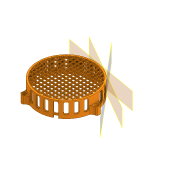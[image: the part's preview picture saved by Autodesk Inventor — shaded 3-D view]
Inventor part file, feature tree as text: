
AUTODESK INVENTOR PART (.ipt)
format: ipt  version: 2020.3 (Build 243373000, 373)  size: 1,350,656 bytes
history: native  units: mm
features: other x23, extrude x10, sketch x7, plane x3, pattern_circular x3
ambient origin geometry x8: Origin, YZ Plane, XZ Plane, XY Plane, X Axis, Y Axis, Z Axis, Center Point
bodies: Body1 (feature_tree)
feature tree (46):
  sketch  "Sketch1"  dims[d0=95.0mm d1=120.0deg]
  extrude  "Extrusion9"  TaperAngle=120.0deg  [1 undecoded]
  extrude  "Extrusion13"  Depth=16.0mm
  extrude  "Extrusion14"  Depth=6.5mm
  extrude  "Extrusion16"  Depth=10.0mm
  extrude  "Extrusion17"  Depth=1.2mm
  plane  "Work Plane5"
  plane  "Work Plane6"
  plane  "Work Plane7"
  sketch  "Sketch12"  dims[d4=3.4mm d5=6.5mm]
  sketch  "Sketch13"  dims[d7=10.0mm d8=3.6mm]
  sketch  "Sketch14"  dims[d9=2.4mm d10=1.2mm]
  extrude  "Extrusion21"  Depth=9.8mm
  extrude  "Extrusion22"  Depth=2.0mm
  extrude  "Extrusion23"  Depth=2.0mm
  sketch  "Sketch15"  dims[d13=30.0mm d15=360.0deg d17=9.8mm]
  sketch  "Sketch16"  dims[d18=12.0mm d19=2.0mm d20=6.0mm d21=2.0mm d23=60.0deg d24=6.1mm d25=8.0mm d26=6.1mm d27=60.0deg d28=3.490659mm d29=3.490659mm d56=40.0mm d57=60.0mm d58=3.2mm d59=1.3mm d60=1.0mm d61=1.0mm d62=1.3mm d64=3.0mm d65=8.0mm d66=6.0mm d74=90.0mm d75=26.0mm d76=0.0mm d83=4.2mm d84=0.0mm d85=8.4mm d86=0.0mm d99=12.5mm d100=0.0mm d101=6.5mm d102=6.0mm d103=6.0mm d104=3.0mm d105=0.0mm d115=4.0mm d116=4.0mm d122=90.0deg d123=90.0deg d124=90.0deg d126=5.5mm d127=5.5mm d128=5.5mm d129=10.0mm d130=0.0mm d131=10.0mm d132=0.0mm d133=10.0mm d134=0.0mm d137=18.0mm d138=2.0mm d141=240.0mm d142=360.0deg d191=2.0mm d192=0.0mm d194=95.0mm d195=90.0mm d198=1.0mm d199=5.0mm d200=1.0mm d201=5.0mm d202=1.0mm d203=5.0mm d204=1.0mm d205=5.0mm d206=1.0mm d207=5.0mm d208=1.0mm d209=5.0mm d210=1.0mm d211=1.0mm d212=5.0mm d213=1.0mm d214=5.0mm d215=1.0mm d216=5.0mm d217=1.0mm d218=5.0mm d219=1.0mm d220=5.0mm d221=1.0mm d222=5.0mm d223=1.0mm d224=5.0mm d225=1.0mm d226=40.0mm d227=360.0deg d229=6.1mm d230=6.0mm d231=0.0mm d232=240.0mm d233=360.0deg d72=0.5mm d73=0.872665mm d106=0.5mm d107=0.872665mm d108=0.5mm d109=0.872665mm d120=0.5mm d121=0.872665mm d125=0.872665mm d139=0.5mm d140=0.872665mm]
  pattern_circular  "Circular Pattern3"  [2 undecoded]
  extrude  "Extrusion27"  TaperAngle=60.0deg  [1 undecoded]
  pattern_circular  "Circular Pattern5"  [2 undecoded]
  extrude  "Extrusion28"  Depth=2.0mm
  pattern_circular  "Circular Pattern6"  [2 undecoded]
  sketch  "Sketch8"  dims[d2=120.0deg d3=16.0mm]
  other  "Work Axis1"
  other  "Work Axis2"
  other  "Work Axis3"
  other  "Work Axis4"
  other  "Work Axis5"
  other  "Work Axis6"
  other  "Work Axis7"
  other  "Work Axis8"
  other  "Work Axis9"
  other  "Work Axis10"
  other  "Work Axis11"
  other  "Work Axis12"
  other  "Work Axis13"
  other  "Work Axis14"
  other  "Work Axis15"
  other  "Work Axis16"
  other  "Work Axis17"
  other  "Work Axis18"
  other  "Work Axis19"
  other  "Work Axis20"
  other  "Work Axis21"
  other  "Work Axis22"
  other  "Work Axis23"
note: 8 required parameter values undecoded (feature->parameter linkage not recoverable at this tier; creation-order binding heuristic only, values carry confidence <= 0.55)
